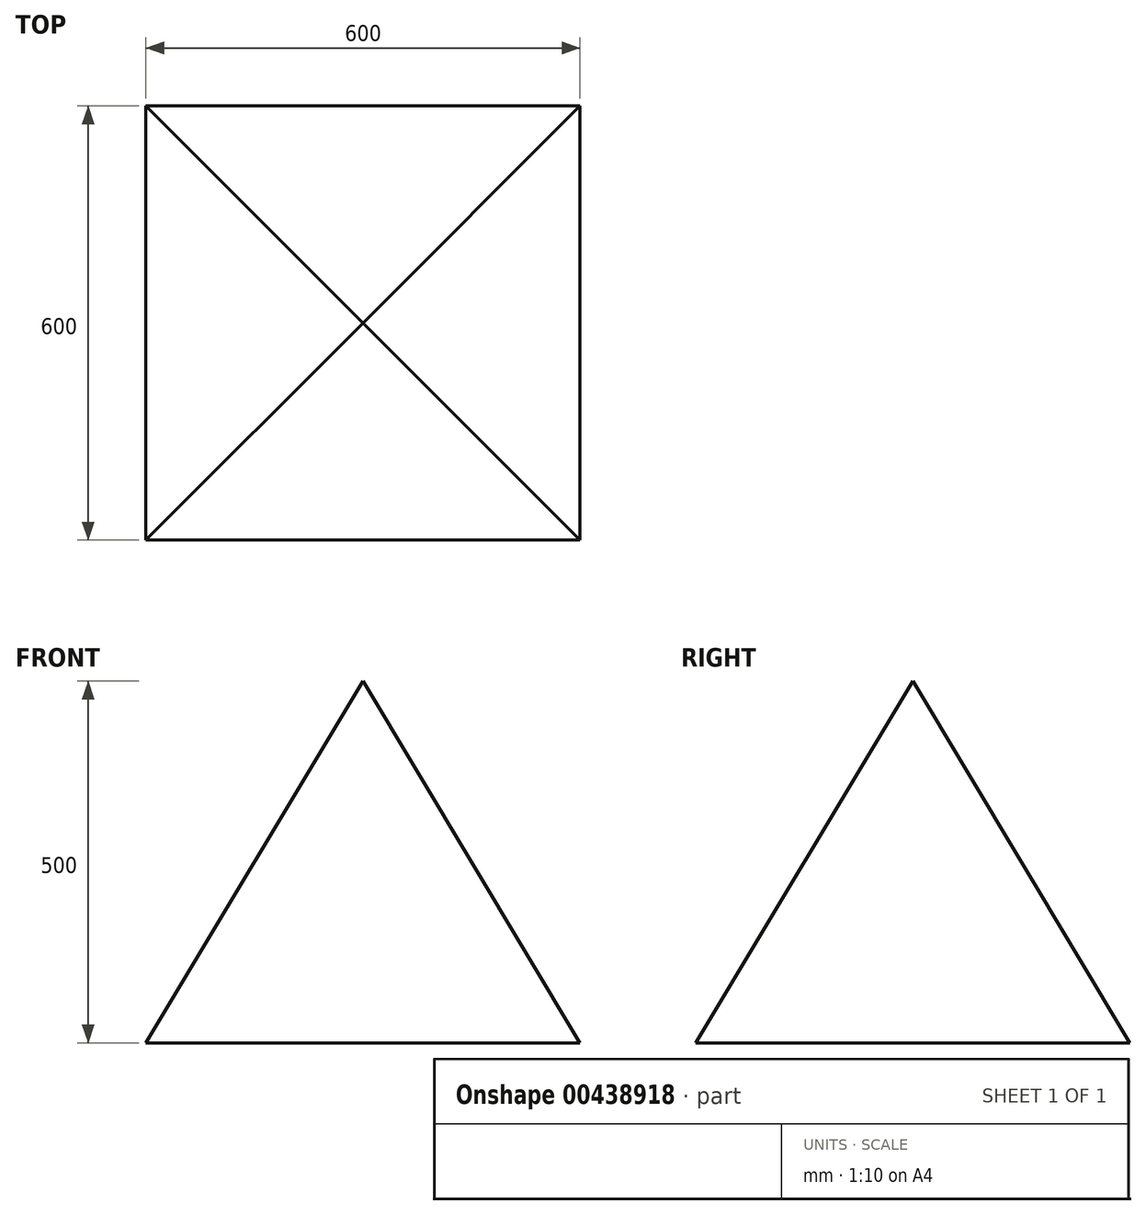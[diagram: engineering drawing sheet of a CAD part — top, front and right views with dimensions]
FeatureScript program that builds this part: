
annotation { "Feature Type Name" : "Feature", "Feature Type Description" : "" }
export const myFeature = defineFeature(function(context is Context, id is Id, definition is map)
    precondition{}
    {
        {
            var Q0;
            Q0=qCreatedBy(makeId("Top.planeOp"),FACE);
            cPlane(context, id + "F0", {"entities" : qUnion([Q0]), "cplaneType" : CPlaneType.OFFSET, "offset" : 500 * mm, "width" : 150 * mm, "height" : 150 * mm});
        }
        {
            var Q0;
            Q0=qCreatedBy(makeId("Top.planeOp"),FACE);
            var sketch = newSketch(context, id + "F1", { "sketchPlane" : qUnion([Q0])});
            skLineSegment(sketch, "E0.bottom", {"start": v(-300, -300) * mm, "end": v(300, -300) * mm});
            skLineSegment(sketch, "E0.top", {"start": v(-300, 300) * mm, "end": v(300, 300) * mm});
            skLineSegment(sketch, "E0.left", {"start": v(-300, -300) * mm, "end": v(-300, 300) * mm});
            skLineSegment(sketch, "E0.right", {"start": v(300, -300) * mm, "end": v(300, 300) * mm});
            skPoint(sketch, "E0.middle", {"position": v(0, 0) * mm});
            skSolve(sketch);
        }
        {
            var Q0;
            Q0=qCreatedBy(id+"F0.planeOp",FACE);
            var sketch = newSketch(context, id + "F2", { "sketchPlane" : qUnion([Q0])});
            skPoint(sketch, "E1", {"position": v(0, 0) * mm});
            skSolve(sketch);
        }
        {
            var Q0;
            Q0=makeQuery(id+"F1.imprint","IMPRINT",FACE,{"disambiguationData":[TD([[makeQuery(id+"F1.imprint","IMPRINT",EDGE,{"derivedFrom":sQuery(id+"F1.wireOp",EDGE,"E0.bottom")}),1.0]])]});
            var Q1;
            Q1=sQuery(id+"F2.wireOp",VERTEX,"E1");
            loft(context, id + "F3", {"sheetProfilesArray" : [{ "sheetProfileEntities" : qUnion([Q0]) }, { "sheetProfileEntities" : qUnion([Q1]) }]});
        }
    });
